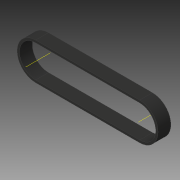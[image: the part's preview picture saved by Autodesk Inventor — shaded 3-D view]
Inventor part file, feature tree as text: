
AUTODESK INVENTOR PART (.ipt)
format: ipt  version: 2019 (Build 230136000, 136)  size: 156,672 bytes
history: native  units: in
note: dims shown in document units (in); Inventor stores cm internally (conversion verified against a paired STEP export)
features: sketch x4, extrude x1, other x1, projected_geometry x1
ambient origin geometry x8: Origin, YZ Plane, XZ Plane, XY Plane, X Axis, Y Axis, Z Axis, Center Point
bodies: Body1 (feature_tree)
feature tree (7):
  sketch  "Sketch1"  dims[d0=0.9023in d1=0.9023in]
  sketch  "Sketch2"  dims[d2=1.4174in]
  extrude  "Extrusion2"  Depth=0.9023in
  sketch  "Sketch5"  dims[d5=2.7165in d9=0.0787in d10=0.0598in d11=0.0299in d12=0.0219in d13=0.0219in d14=0.0059in d15=0.0059in d20=0.3346in d21=0.0in d22=0.0787in d23=0.0598in d24=0.0299in d25=0.0219in d26=0.0219in d27=0.0059in d28=0.0059in d29=0.0299in d30=0.0394in d31=0.0787in d32=0.0232in d34=0.0219in d35=0.0in d36=0.0in d37=0.0059in d38=0.0022in d39=0.0022in d40=0.0in d41=0.0in d42=0.0081in d43=0.0081in d44=0.0299in]
  other  "Work Axis1"
  sketch  "Sketch4"  dims[d3=1.4174in]
  projected_geometry  "Projected Loop1"
